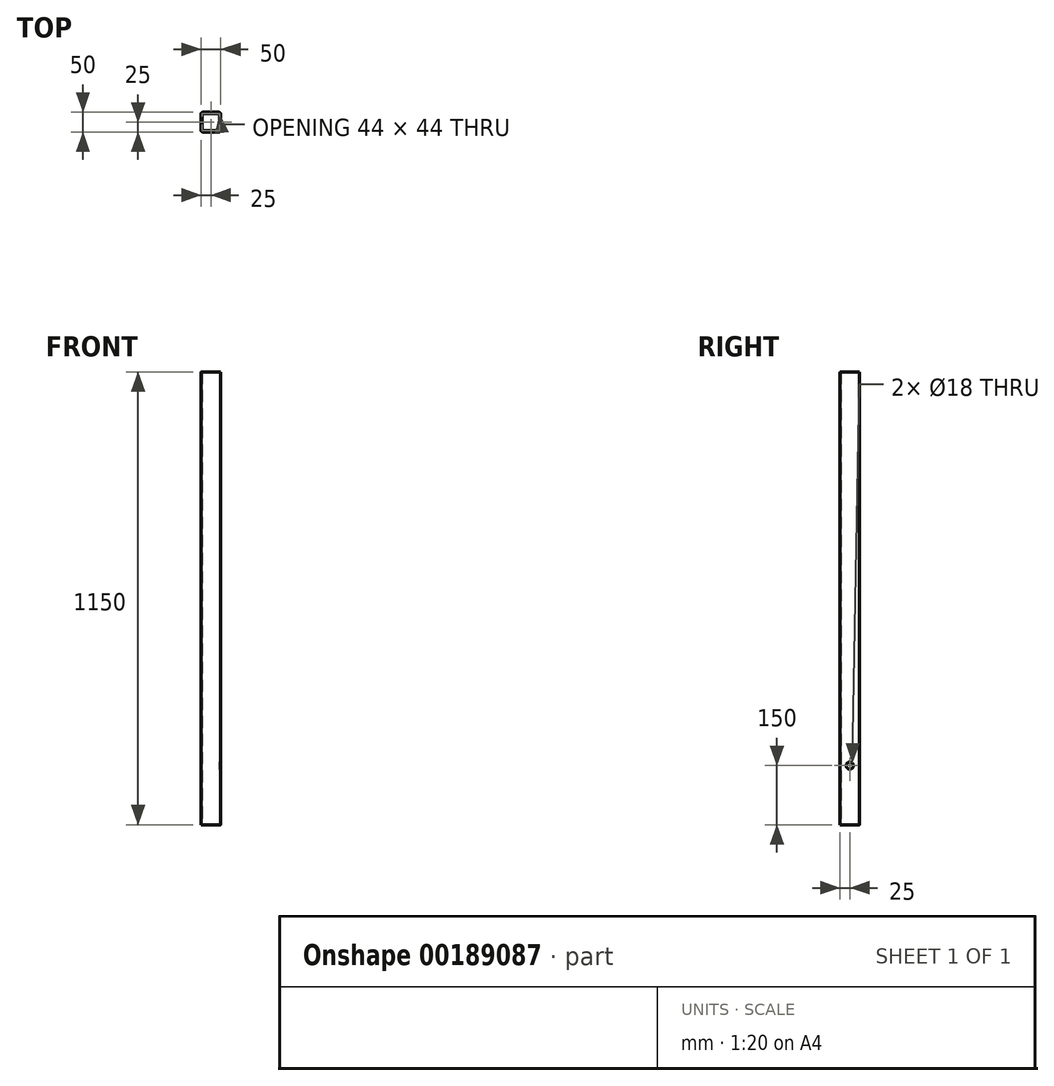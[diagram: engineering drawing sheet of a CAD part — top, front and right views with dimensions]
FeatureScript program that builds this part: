
annotation { "Feature Type Name" : "Feature", "Feature Type Description" : "" }
export const myFeature = defineFeature(function(context is Context, id is Id, definition is map)
    precondition{}
    {
        {
            var Q0;
            Q0=qCreatedBy(makeId("Top.planeOp"),FACE);
            var sketch = newSketch(context, id + "F0", { "sketchPlane" : qUnion([Q0])});
            skLineSegment(sketch, "E0.bottom", {"start": v(25, 25) * mm, "end": v(-25, 25) * mm});
            skLineSegment(sketch, "E0.top", {"start": v(25, -25) * mm, "end": v(-25, -25) * mm});
            skLineSegment(sketch, "E0.left", {"start": v(25, 25) * mm, "end": v(25, -25) * mm});
            skLineSegment(sketch, "E0.right", {"start": v(-25, 25) * mm, "end": v(-25, -25) * mm});
            skPoint(sketch, "E0.middle", {"position": v(0, 0) * mm});
            skLineSegment(sketch, "E1.0", {"start": v(22, 22) * mm, "end": v(-22, 22) * mm});
            skLineSegment(sketch, "E1.1", {"start": v(22, 22) * mm, "end": v(22, -22) * mm});
            skLineSegment(sketch, "E1.2", {"start": v(22, -22) * mm, "end": v(-22, -22) * mm});
            skLineSegment(sketch, "E1.3", {"start": v(-22, 22) * mm, "end": v(-22, -22) * mm});
            skSolve(sketch);
        }
        {
            var Q0;
            Q0=makeQuery(id+"F0.imprint","IMPRINT",FACE,{"disambiguationData":[TD([[makeQuery(id+"F0.imprint","IMPRINT",EDGE,{"derivedFrom":sQuery(id+"F0.wireOp",EDGE,"E0.bottom")}),1.0]])]});
            extrude(context, id + "F1", {"entities" : qUnion([Q0]), "depth" : 1150 * mm});
        }
        {
            var Q0;
            Q0=makeQuery(id+"F1.opExtrude","SWEPT_EDGE",EDGE,{"disambiguationData":[OSD([sQuery(id+"F0.wireOp",EDGE,"E1.0"),sQuery(id+"F0.wireOp",EDGE,"E1.1")])]});
            var Q1;
            Q1=makeQuery(id+"F1.opExtrude","SWEPT_EDGE",EDGE,{"disambiguationData":[OSD([sQuery(id+"F0.wireOp",EDGE,"E1.2"),sQuery(id+"F0.wireOp",EDGE,"E1.3")])]});
            var Q2;
            Q2=makeQuery(id+"F1.opExtrude","SWEPT_EDGE",EDGE,{"disambiguationData":[OSD([sQuery(id+"F0.wireOp",EDGE,"E1.0"),sQuery(id+"F0.wireOp",EDGE,"E1.3")])]});
            var Q3;
            Q3=makeQuery(id+"F1.opExtrude","SWEPT_EDGE",EDGE,{"disambiguationData":[OSD([sQuery(id+"F0.wireOp",EDGE,"E1.1"),sQuery(id+"F0.wireOp",EDGE,"E1.2")])]});
            fillet(context, id + "F2", {"entities" : qUnion([Q0, Q1, Q2, Q3]), "radius" : 2 * mm, "tangentPropagation" : true, "allowEdgeOverflow" : false});
        }
        {
            var Q0;
            Q0=makeQuery(id+"F1.opExtrude","SWEPT_EDGE",EDGE,{"disambiguationData":[OSD([sQuery(id+"F0.wireOp",EDGE,"E0.bottom"),sQuery(id+"F0.wireOp",EDGE,"E0.right")])]});
            var Q1;
            Q1=makeQuery(id+"F1.opExtrude","SWEPT_EDGE",EDGE,{"disambiguationData":[OSD([sQuery(id+"F0.wireOp",EDGE,"E0.bottom"),sQuery(id+"F0.wireOp",EDGE,"E0.left")])]});
            var Q2;
            Q2=makeQuery(id+"F1.opExtrude","SWEPT_EDGE",EDGE,{"disambiguationData":[OSD([sQuery(id+"F0.wireOp",EDGE,"E0.top"),sQuery(id+"F0.wireOp",EDGE,"E0.right")])]});
            var Q3;
            Q3=makeQuery(id+"F1.opExtrude","SWEPT_EDGE",EDGE,{"disambiguationData":[OSD([sQuery(id+"F0.wireOp",EDGE,"E0.top"),sQuery(id+"F0.wireOp",EDGE,"E0.left")])]});
            fillet(context, id + "F3", {"entities" : qUnion([Q0, Q1, Q2, Q3]), "radius" : 5 * mm, "tangentPropagation" : true, "allowEdgeOverflow" : false});
        }
        {
            var Q0;
            Q0=makeQuery(id+"F1.opExtrude","SWEPT_FACE",FACE,{"disambiguationData":[OSD([sQuery(id+"F0.wireOp",EDGE,"E0.left")])]});
            var sketch = newSketch(context, id + "F4", { "sketchPlane" : qUnion([Q0])});
            skLineSegment(sketch, "E2", {"start": v(0, 0) * mm, "end": v(0, 150) * mm, "construction": true});
            skPoint(sketch, "E3", {"position": v(0, 150) * mm});
            skSolve(sketch);
        }
        {
            var Q0;
            Q0=sQuery(id+"F4.wireOp",VERTEX,"E3");
            var Q1;
            Q1=makeQuery(id+"F1.opExtrude","SWEPT_BODY",BODY,{"disambiguationData":[OSD([sQuery(id+"F0.wireOp",EDGE,"E0.bottom"),sQuery(id+"F0.wireOp",EDGE,"E0.top"),sQuery(id+"F0.wireOp",EDGE,"E0.left"),sQuery(id+"F0.wireOp",EDGE,"E0.right"),sQuery(id+"F0.wireOp",EDGE,"E1.0"),sQuery(id+"F0.wireOp",EDGE,"E1.1"),sQuery(id+"F0.wireOp",EDGE,"E1.2"),sQuery(id+"F0.wireOp",EDGE,"E1.3")])]});
            hole(context, id + "F5", {"style" : HoleStyle.SIMPLE, "endStyle" : HoleEndStyle.THROUGH, "standardTappedOrClearance" : lookupTablePath({ "standard" : "ISO", "size" : "18", "type" : "Drilled" }), "standardBlindInLast" : lookupTablePath({ "standard" : "ISO", "size" : "18", "type" : "Drilled" }), "holeDiameter" : 18 * mm, "startFromSketch" : true, "locations" : qUnion([Q0]), "scope" : qUnion([Q1]), "isTappedThrough" : true});
        }
    });
